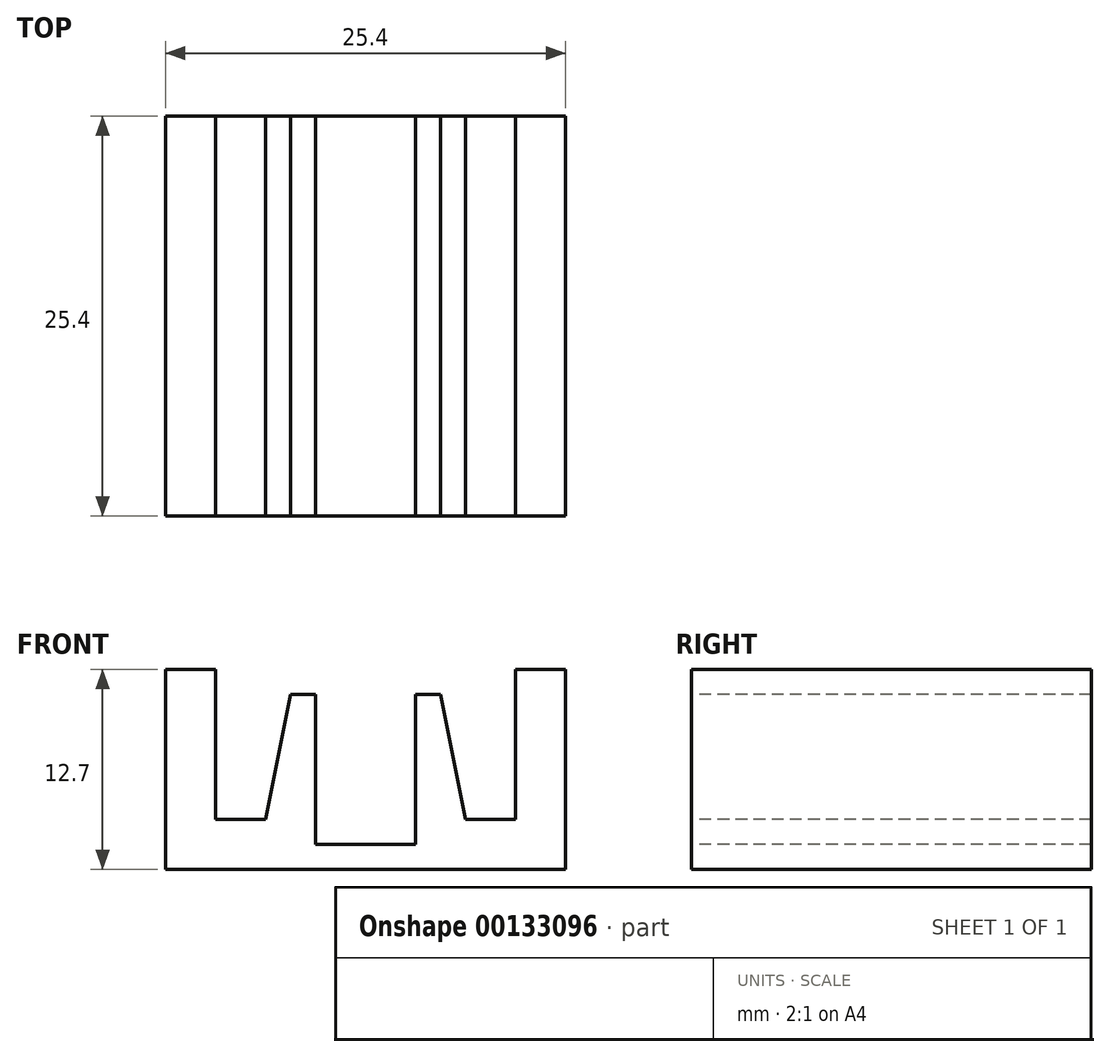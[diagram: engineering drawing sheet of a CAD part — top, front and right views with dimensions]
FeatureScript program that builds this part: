
annotation { "Feature Type Name" : "Feature", "Feature Type Description" : "" }
export const myFeature = defineFeature(function(context is Context, id is Id, definition is map)
    precondition{}
    {
        {
            var Q0;
            Q0=qCreatedBy(makeId("Front.planeOp"),FACE);
            var sketch = newSketch(context, id + "F0", { "sketchPlane" : qUnion([Q0])});
            skLineSegment(sketch, "E0.bottom", {"start": v(-12.7, 6.35) * mm, "end": v(12.7, 6.35) * mm});
            skLineSegment(sketch, "E0.top", {"start": v(-12.7, -6.35) * mm, "end": v(12.7, -6.35) * mm});
            skLineSegment(sketch, "E0.left", {"start": v(-12.7, 6.35) * mm, "end": v(-12.7, -6.35) * mm});
            skLineSegment(sketch, "E0.right", {"start": v(12.7, 6.35) * mm, "end": v(12.7, -6.35) * mm});
            skPoint(sketch, "E0.middle", {"position": v(0, 0) * mm});
            skSolve(sketch);
        }
        {
            var Q0;
            Q0 = qSketchRegion(id + "F0", true);
            extrude(context, id + "F1", {"entities" : qUnion([Q0]), "depth" : 25.4 * mm});
        }
        {
            var Q0;
            Q0=makeQuery(id+"F1.opExtrude","CAP_FACE",FACE,{"disambiguationData":[OSD([sQuery(id+"F0.wireOp",EDGE,"E0.bottom"),sQuery(id+"F0.wireOp",EDGE,"E0.top"),sQuery(id+"F0.wireOp",EDGE,"E0.left"),sQuery(id+"F0.wireOp",EDGE,"E0.right")])],"isStart":false});
            var sketch = newSketch(context, id + "F2", { "sketchPlane" : qUnion([Q0])});
            skLineSegment(sketch, "E1.bottom", {"start": v(3.18, 4.76) * mm, "end": v(-3.17, 4.76) * mm});
            skLineSegment(sketch, "E1.top", {"start": v(3.17, -4.76) * mm, "end": v(-3.18, -4.76) * mm});
            skLineSegment(sketch, "E1.left", {"start": v(3.18, 4.76) * mm, "end": v(3.17, -4.76) * mm});
            skLineSegment(sketch, "E1.right", {"start": v(-3.17, 4.76) * mm, "end": v(-3.18, -4.76) * mm});
            skPoint(sketch, "E1.middle", {"position": v(0, 0) * mm});
            skSolve(sketch);
        }
        {
            var Q0;
            Q0 = qSketchRegion(id + "F2", true);
            extrude(context, id + "F3", {"entities" : qUnion([Q0]), "operationType" : NewBodyOperationType.REMOVE, "oppositeDirection" : true, "depth" : 25.4 * mm});
        }
        {
            var Q0;
            Q0=makeQuery(id+"F1.opExtrude","CAP_FACE",FACE,{"disambiguationData":[OSD([sQuery(id+"F0.wireOp",EDGE,"E0.bottom"),sQuery(id+"F0.wireOp",EDGE,"E0.top"),sQuery(id+"F0.wireOp",EDGE,"E0.left"),sQuery(id+"F0.wireOp",EDGE,"E0.right")])],"isStart":false});
            var sketch = newSketch(context, id + "F4", { "sketchPlane" : qUnion([Q0])});
            skLineSegment(sketch, "E2", {"start": v(-3.17, 4.76) * mm, "end": v(-4.76, 4.76) * mm});
            skPoint(sketch, "E2.endSnap0", {"position": v(0, 4.76) * mm});
            skLineSegment(sketch, "E3", {"start": v(-4.76, 4.76) * mm, "end": v(-6.35, -3.18) * mm});
            skLineSegment(sketch, "E4", {"start": v(-6.35, -3.18) * mm, "end": v(-9.53, -3.18) * mm});
            skLineSegment(sketch, "E5", {"start": v(-9.53, -3.18) * mm, "end": v(-9.53, 6.35) * mm});
            skLineSegment(sketch, "E6", {"start": v(-9.53, 6.35) * mm, "end": v(0, 6.35) * mm});
            skLineSegment(sketch, "E7.MirrorCS", {"start": v(6.35, -3.18) * mm, "end": v(9.53, -3.18) * mm});
            skLineSegment(sketch, "E8.MirrorCS", {"start": v(3.17, 4.76) * mm, "end": v(4.76, 4.76) * mm});
            skLineSegment(sketch, "E9.MirrorCS", {"start": v(9.53, -3.18) * mm, "end": v(9.53, 6.35) * mm});
            skLineSegment(sketch, "E10.MirrorCS", {"start": v(4.76, 4.76) * mm, "end": v(6.35, -3.18) * mm});
            skLineSegment(sketch, "E11.MirrorCS", {"start": v(9.53, 6.35) * mm, "end": v(0, 6.35) * mm});
            skLineSegment(sketch, "E12", {"start": v(-3.17, 4.76) * mm, "end": v(3.17, 4.76) * mm});
            skSolve(sketch);
        }
        {
            var Q0;
            Q0 = qSketchRegion(id + "F4", true);
            extrude(context, id + "F5", {"entities" : qUnion([Q0]), "operationType" : NewBodyOperationType.REMOVE, "endBound" : BoundingType.THROUGH_ALL, "oppositeDirection" : true, "depth" : 25.4 * mm});
        }
    });
